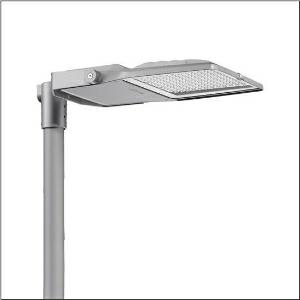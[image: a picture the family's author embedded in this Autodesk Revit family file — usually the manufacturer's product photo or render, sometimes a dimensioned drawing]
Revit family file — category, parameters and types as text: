
# Revit family: floodlight_fl_21_iq_midi___pl61_5xa7781f2c3a_20a4
name_source: partatom
category: Lighting Fixtures
units: mm (PartAtom-declared; Revit-internal decimal feet)

## family parameters
Cut with Voids When Loaded = No
Host = Face
Light Source = No
Part Type = Normal
Room Calculation Point = No
Round Connector Dimension = Use Diameter
Shared = No

## types (1)
- --- (1 x LED, 35100 lm, 270.2 W, 3000K)
    Apparent Load = 270 VA
    CIE Flux Codes = 33 65 98 100 100
    Color Rendering = 70
    Color Temperature = 3000K
    Default Elevation = 1800 mm
    Description = Floodlight FL 21 iQ midi, floodlight, primary light control with lens, of PMMA, primary optical cover: protective disc, of toughened safety glass, transparent, light distribution: PL61, light emission: direct distribution, installation type: surface-mounted, LED, High Power LED, rated luminous flux: 35.100lm, luminous efficacy: 130lm/W, light colour: 730, colour temperature: 3000K, control gear: iQ Comfort/DALI, control: optimised constant luminous flux control (CLO 2.0), Desk-Remote (wireless, voltage-free reading and setting of iQ features in the workshop via application-optimized NFC function/RFID function), Light-Fading, Smart-Wire, Night-Set, Lumen-Switch, Temp-Guard, Auto-Match, with terminal, 6-pole, mains connection: 220..240V, AC, 50/60Hz, start of lifetime: 270W, end of service life: 287W, reduction: 117W, luminaire housing, of diecast aluminium, powder-coated, Siteco® metallic grey (DB 702S), corrosivity category C5 mid according to DIN EN ISO 12944, suitable for swimming pools, chlorine-resistant, sealing non-destructively replaceable, please order mast flange separately, mast bracket, of steel, galvanised, powder-coated, Siteco® metallic grey (DB 702S), protection rating (complete): IP66, insulation class (complete): insulation class II (safety insulation), certification: CE, ENEC, VDE, protection symbol: D, impact resistance: IK08, permissible operating ambient temperature: -40..+40°C, permissible operating ambient temperature for outdoor applications: -40..+50°C, standard: DIN EN 12944, LABS conformity tested according to VDMA 24364:2018-05, packaging unit: 1 piece

Light Distribution: PL61
    Height = 76 mm
    Lamp = 1 x LED
    Lamp Light Flux = 35100 lm
    Lamp Power = 270.2 W
    Lamp count = 1
    Length = 657 mm
    Luminous efficacy = 130 lm/W
    Manufacturer = Siteco
    ModVariant = No
    Model = 5XA7781F2C3A
    Number of Poles = 1
    OnlyDefault = Yes
    Power Factor = 1
    Product Name = Floodlight FL 21 iQ midi | PL61
    Product group = floodlight | pylon annexe
    ProductGroupID = 6200
    Protection Class = Protection class II
    Protection Degree = IP 66
    RLX_Detail_Level = 1
    RLX_Emergency_Light_Flux = 0 lm
    RLX_Emergency_Type = 0
    RLX_Emergency_Type_DB = No
    RlxData = <blob elided: 153709 chars, md5=5055dd14>
    Socket = socket
    Standby Power = 0 W
    System Light Flux = 35100 lm
    System Power = 270 W
    Type Comments = factory setting: luminous flux: 100 % | dim-lin: 254 | 620 mA
    Type Image = l_1007123.jpg
    URL = http://relux.com
    VarID = @adj_108488
    Voltage = 0 V
    Weight = 0.00 kg
    Width = 442 mm

## geometry (parser evidence)
native form markers: Blend x4, Sweep x14
no freeform markers — native parametric forms only
